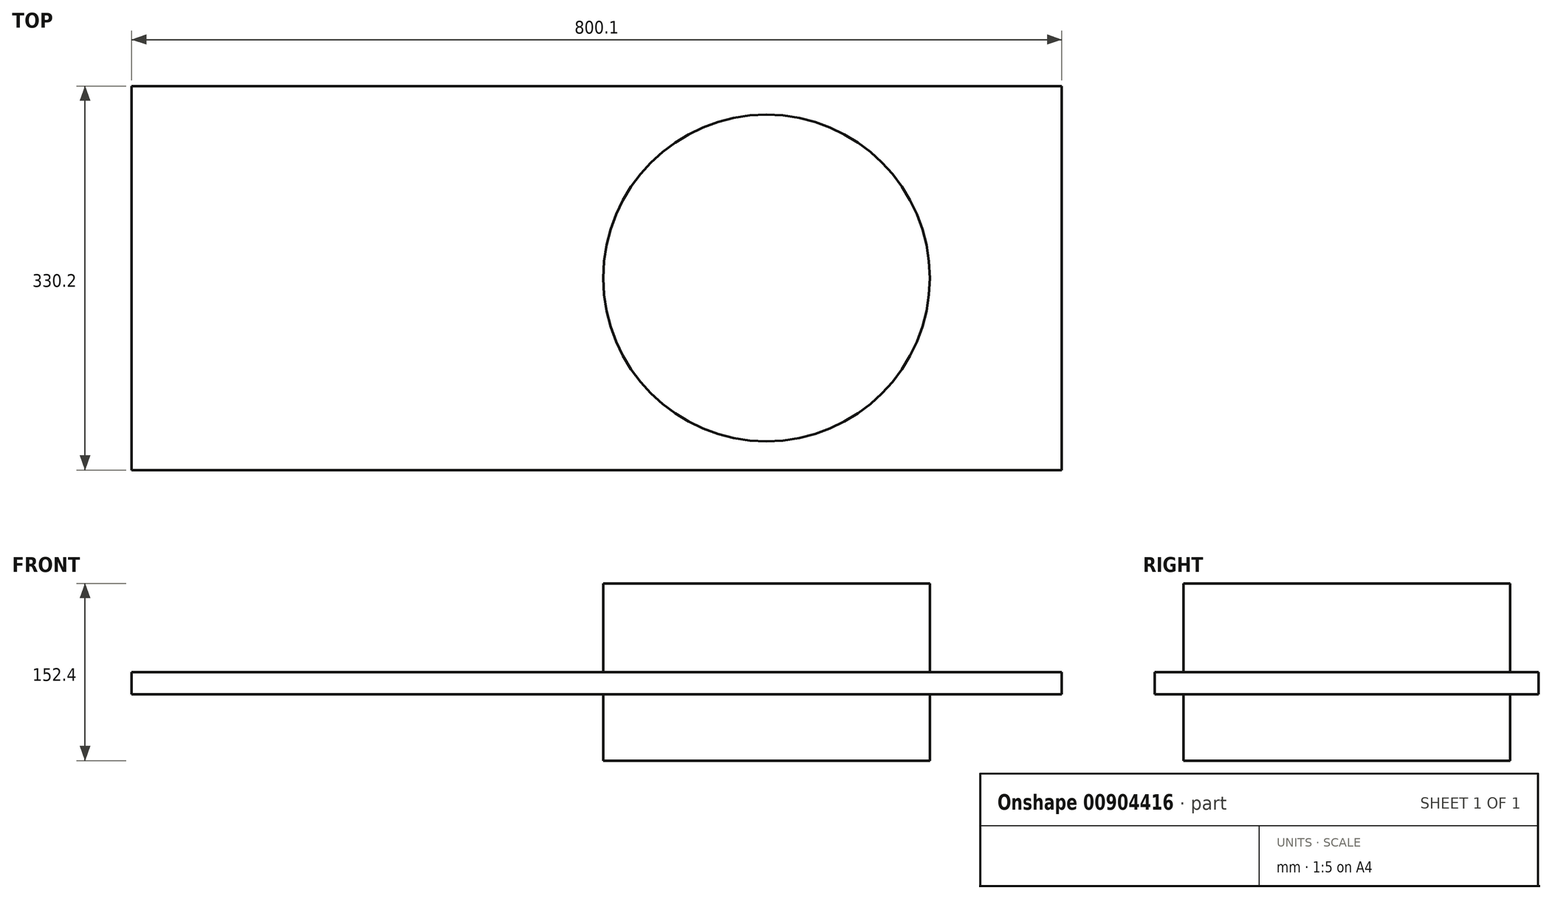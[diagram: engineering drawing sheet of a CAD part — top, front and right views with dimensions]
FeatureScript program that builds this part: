
annotation { "Feature Type Name" : "Feature", "Feature Type Description" : "" }
export const myFeature = defineFeature(function(context is Context, id is Id, definition is map)
    precondition{}
    {
        {
            var Q0;
            Q0=qCreatedBy(makeId("Top.planeOp"),FACE);
            var sketch = newSketch(context, id + "F0", { "sketchPlane" : qUnion([Q0])});
            skLineSegment(sketch, "E0.bottom", {"start": v(0, 0) * mm, "end": v(800.1, 0) * mm});
            skLineSegment(sketch, "E0.top", {"start": v(0, 330.2) * mm, "end": v(800.1, 330.2) * mm});
            skLineSegment(sketch, "E0.left", {"start": v(0, 0) * mm, "end": v(0, 330.2) * mm});
            skLineSegment(sketch, "E0.right", {"start": v(800.1, 0) * mm, "end": v(800.1, 330.2) * mm});
            skSolve(sketch);
        }
        {
            var Q0;
            Q0 = qSketchRegion(id + "F0", true);
            extrude(context, id + "F1", {"entities" : qUnion([Q0]), "depth" : 19.05 * mm, "offsetDistance" : 25.4 * mm});
        }
        {
            var Q0;
            Q0=makeQuery(id+"F1.opExtrude","CAP_FACE",FACE,{"disambiguationData":[OSD([sQuery(id+"F0.wireOp",EDGE,"E0.bottom"),sQuery(id+"F0.wireOp",EDGE,"E0.top"),sQuery(id+"F0.wireOp",EDGE,"E0.left"),sQuery(id+"F0.wireOp",EDGE,"E0.right")])],"isStart":false});
            var sketch = newSketch(context, id + "F2", { "sketchPlane" : qUnion([Q0])});
            skCircle(sketch, "E1", {"center": v(546.1, 165.1) * mm, "radius": 140.46 * mm});
            skLineSegment(sketch, "E2", {"start": v(800.1, 165.1) * mm, "end": v(12.61, 165.1) * mm, "construction": true});
            skSolve(sketch);
        }
        {
            var Q0;
            Q0 = qSketchRegion(id + "F2", true);
            extrude(context, id + "F3", {"entities" : qUnion([Q0]), "operationType" : NewBodyOperationType.ADD, "oppositeDirection" : true, "depth" : 76.2 * mm, "offsetDistance" : 25.4 * mm, "hasSecondDirection" : true, "secondDirectionOppositeDirection" : false, "secondDirectionDepth" : 76.2 * mm});
        }
    });
